# Revit family: Haworth_Massimosistema_Sofa_TwoArms_HighLow
name_source: partatom
category: Furniture
revit_build: Autodesk Revit 2018 (Build: 20170223_1515(x64)
units: mm (PartAtom-declared; Revit-internal decimal feet)

## family parameters
Always vertical = Yes
Cut with Voids When Loaded = No
OmniClass Number = 23.40.20.00
OmniClass Title = General Furniture and Specialties
Room Calculation Point = No
Shared = No
Work Plane-Based = No

## types (2) — shared parameters
Actual Depth = 39 1/4"
Actual Height = 33 3/4"
Arm Width = 8 5/8"
Assembly Code = E2020200
Frame Finish = Haworth _ Paint _ Metallic Gunmetal
High Arm = 28"
Low Arm = 22 3/4"
Manufacturer = Haworth
Size = Verify Final Dim. w/ Haworth
URL = http://www.haworth.com
URL - Product = http://www.haworth.com
Version = 1
Warranty = https://www.haworth.com

## per-type parameters (varying)
| type | Actual Width | Cushion Width | Description | Seat Width | Three Seats | Two Seat Control | Two Seats |
| HCPF-MSS3 | 112 1/2" | 95 1/4" | Haworth Massimosistema Sofa - One Low, High Arms - Three Seats | 31 3/4" | Yes | Yes | No |
| HCPF-MSS2 | 80 1/4" | 63" | Haworth Massimosistema Sofa - One Low, High Arms - Two Seats | 31 1/2" | No | No | Yes |

note: column(s) folded — value = type name in every type: Model

## geometry (parser evidence)
native form markers: Sweep x6
no freeform markers — native parametric forms only
